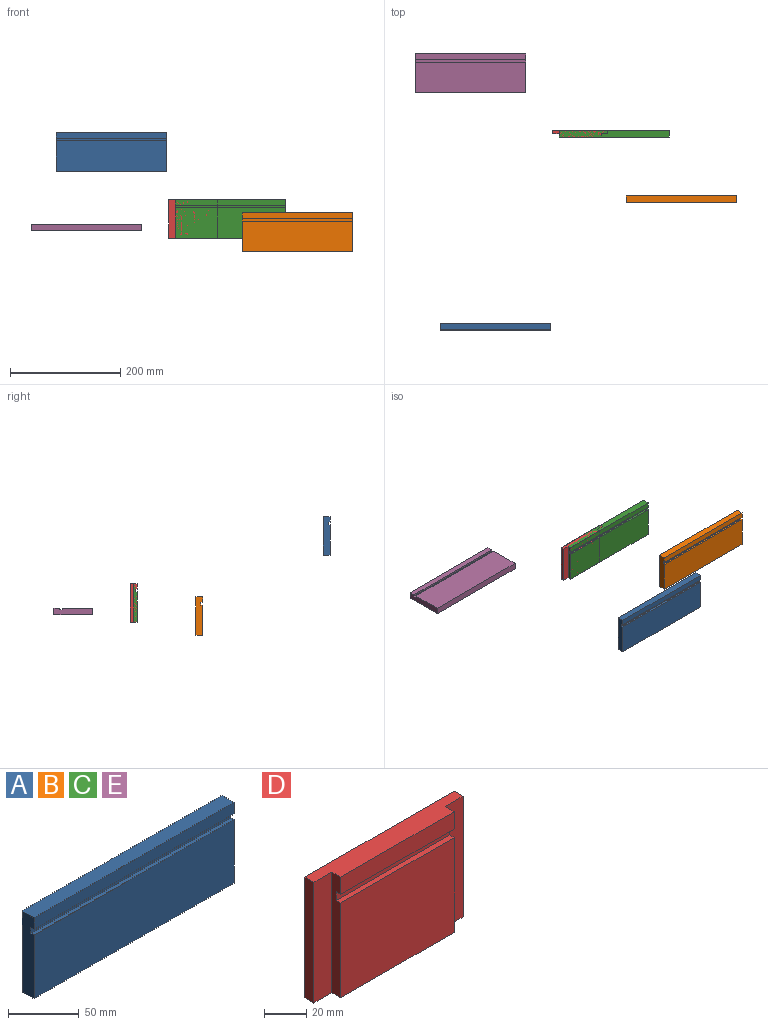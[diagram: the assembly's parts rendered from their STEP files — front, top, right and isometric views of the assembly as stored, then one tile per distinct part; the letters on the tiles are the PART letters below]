
ASSEMBLY  parts=5 mates=2
PART A: 10 faces, bbox 200x12x70 mm
  f0: plane 200x55mm, normal (0,-1,0), area 11000mm2, adj f1,f7,f8,f9
  f1: plane 200x12mm, normal (0,0,-1), area 2400mm2, adj f0,f2,f8,f9
  f2: plane 200x70mm, normal (0,1,0), area 14000mm2, adj f1,f3,f8,f9
  f3: plane 200x12mm, normal (0,0,1), area 2400mm2, adj f2,f4,f8,f9
  f4: plane 200x10mm, normal (0,-1,0), area 2000mm2, adj f3,f5,f8,f9
  f5: plane 200x3mm, normal (0,0,-1), area 600mm2, adj f4,f6,f8,f9
  f6: plane 200x5mm, normal (0,-1,0), area 1000mm2, adj f5,f7,f8,f9
  f7: plane 200x3mm, normal (0,0,1), area 600mm2, adj f0,f6,f8,f9
  f8: plane 70x12mm, normal (1,0,0), area 825mm2, adj f0,f1,f2,f3,f4,f5,f6,f7
  f9: plane 70x12mm, normal (-1,0,0), area 825mm2, adj f0,f1,f2,f3,f4,f5,f6,f7
PART B: same geometry as A
PART C: same geometry as A
PART D: 14 faces, bbox 100x12x70 mm
  f0: plane 100x12mm, normal (0,0,1), area 1056mm2, adj f1,f7,f8,f9,f10,f11,f12,f13
  f1: plane 76x10mm, normal (0,-1,0), area 760mm2, adj f0,f3,f10,f12
  f2: plane 76x55mm, normal (0,-1,0), area 4180mm2, adj f5,f6,f10,f12
  f3: plane 76x3mm, normal (0,0,-1), area 228mm2, adj f1,f4,f10,f12
  f4: plane 76x5mm, normal (0,-1,0), area 380mm2, adj f3,f5,f10,f12
  f5: plane 76x3mm, normal (0,0,1), area 228mm2, adj f2,f4,f10,f12
  f6: plane 100x12mm, normal (0,0,-1), area 1056mm2, adj f2,f7,f8,f9,f10,f11,f12,f13
  f7: plane 100x70mm, normal (0,1,0), area 7000mm2, adj f0,f6,f8,f9
  f8: plane 70x6mm, normal (1,0,0), area 420mm2, adj f0,f6,f7,f13
  f9: plane 70x6mm, normal (-1,0,0), area 420mm2, adj f0,f6,f7,f11
  f10: plane 70x6mm, normal (-1,0,0), area 405mm2, adj f0,f1,f2,f3,f4,f5,f6,f11
  f11: plane 70x12mm, normal (0,-1,0), area 840mm2, adj f0,f6,f9,f10
  f12: plane 70x6mm, normal (1,0,0), area 405mm2, adj f0,f1,f2,f3,f4,f5,f6,f13
  f13: plane 70x12mm, normal (0,-1,0), area 840mm2, adj f0,f6,f8,f12
PART E: same geometry as A
PLACE A t=(2.53,-533.42,558.46)mm
PLACE B t=(340.92,-301.6,412.59)mm
PLACE C t=(218.86,-182.59,436.58)mm
PLACE D t=(206.86,-170.59,436.58)mm
PLACE E rot(axis=(-1,0,0),90deg) t=(-42.26,-101.56,461.81)mm
MATE fastened C.f0 <-> D.f2  axis (0,-1,0) through (218.86,-182.59,464.08)mm
MATE cylindrical E.f0 <-> E.f0  axis (0,0,1) through (57.74,-74.06,461.81)mm
